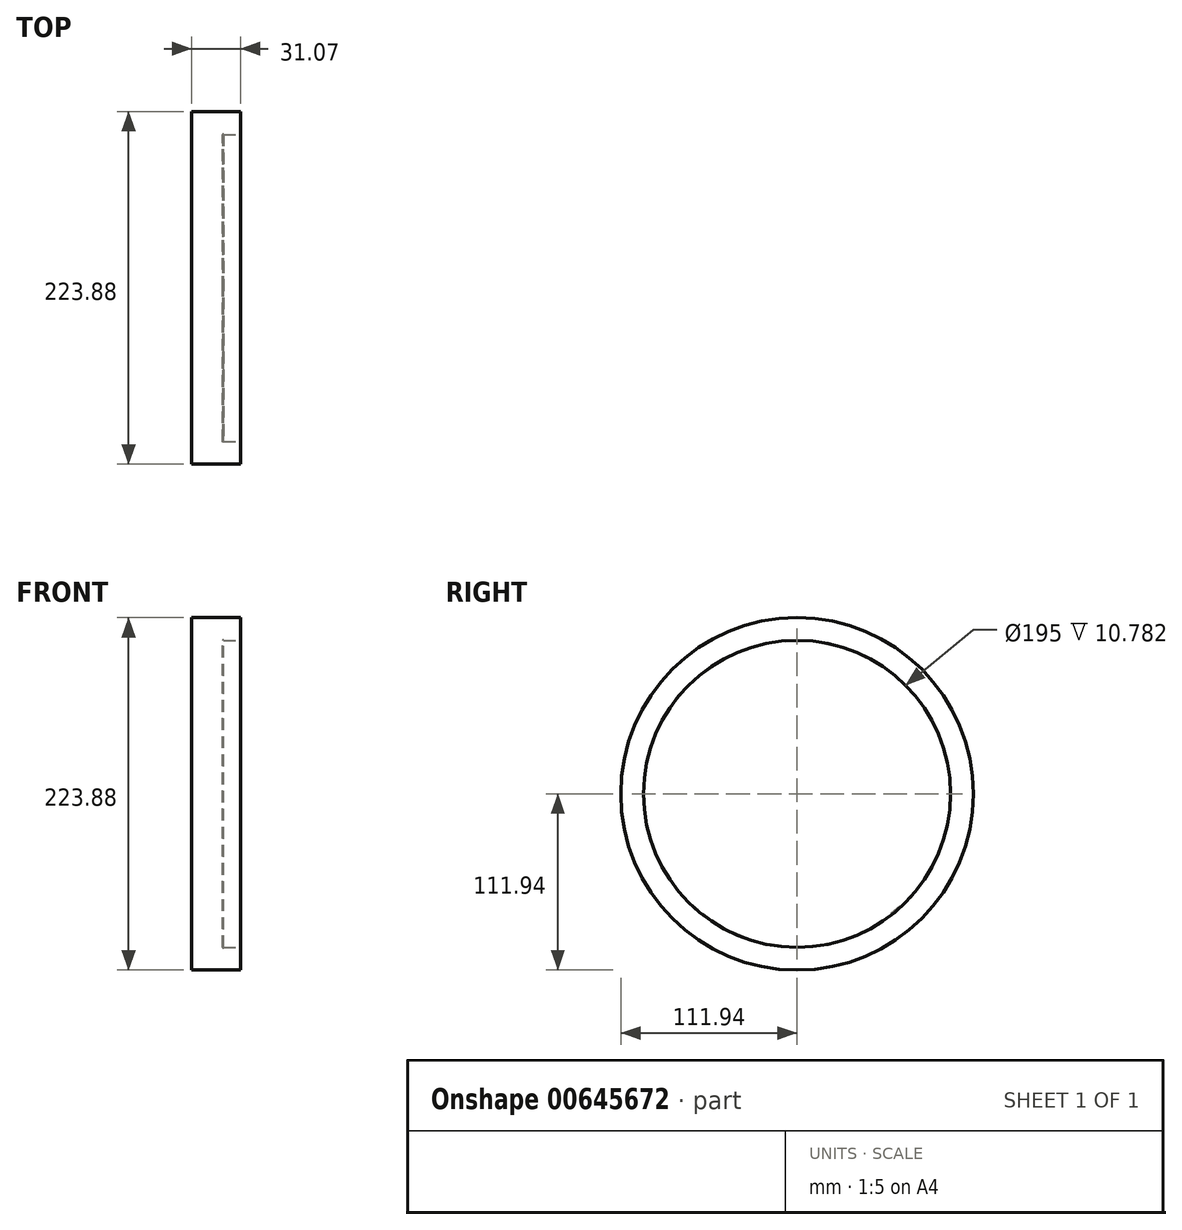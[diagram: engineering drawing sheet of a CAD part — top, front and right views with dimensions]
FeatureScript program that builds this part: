
annotation { "Feature Type Name" : "Feature", "Feature Type Description" : "" }
export const myFeature = defineFeature(function(context is Context, id is Id, definition is map)
    precondition{}
    {
        {
            var Q0;
            Q0=qCreatedBy(makeId("Front.planeOp"),FACE);
            var sketch = newSketch(context, id + "F0", { "sketchPlane" : qUnion([Q0])});
            skLineSegment(sketch, "E0", {"start": v(0, 0) * mm, "end": v(0, 97.4) * mm});
            skLineSegment(sketch, "E1", {"start": v(0.73, 97.63) * mm, "end": v(0.82, 97.5) * mm});
            skLineSegment(sketch, "E2", {"start": v(0, 98.67) * mm, "end": v(1.33, 98.67) * mm, "construction": true});
            skPoint(sketch, "E3.visualSharp", {"position": v(0, 98.67) * mm});
            skArc(sketch, "E3.filletArc", {"start": v(0.73, 97.63) * mm, "mid": v(0.28, 97.78) * mm, "end": v(0, 97.4) * mm});
            skLineSegment(sketch, "E4", {"start": v(0.4, 97.4) * mm, "end": v(0.4, 98.29) * mm, "construction": true});
            skPoint(sketch, "E5", {"position": v(0.4, 97.8) * mm});
            skLineSegment(sketch, "E6", {"start": v(0.82, 97.5) * mm, "end": v(11.6, 97.5) * mm});
            skLineSegment(sketch, "E7", {"start": v(11.6, 111.94) * mm, "end": v(11.6, 97.5) * mm});
            skLineSegment(sketch, "E8", {"start": v(11.6, 111.94) * mm, "end": v(-19.47, 111.94) * mm});
            skLineSegment(sketch, "E9", {"start": v(0, 0) * mm, "end": v(-19.47, 0) * mm});
            skLineSegment(sketch, "E10", {"start": v(-19.47, 0) * mm, "end": v(-19.47, 111.94) * mm});
            skSolve(sketch);
        }
        {
            var Q0;
            Q0 = qSketchRegion(id + "F0", true);
            var Q1;
            Q1=sQuery(id+"F0.wireOp",EDGE,"E9");
            revolve(context, id + "F1", {"entities" : qUnion([Q0]), "axis" : qUnion([Q1]), "revolveType" : RevolveType.FULL});
        }
    });
